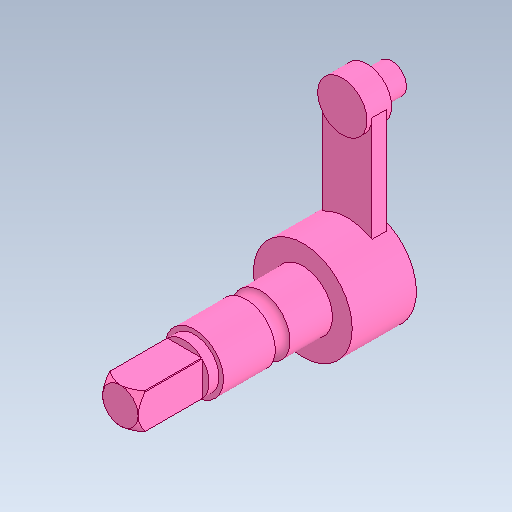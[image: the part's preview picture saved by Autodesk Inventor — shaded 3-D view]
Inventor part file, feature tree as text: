
AUTODESK INVENTOR PART (.ipt)
format: ipt  version: 2020.5 (Build 245400000, 400)  size: 203,264 bytes
history: native  units: mm
features: sketch x9, extrude x8, other x2, mirror x1, chamfer x1, revolve x1, projected_geometry x1
ambient origin geometry x8: Origin, YZ Plane, XZ Plane, XY Plane, X Axis, Y Axis, Z Axis, Center Point
bodies: Solid1 (feature_tree)
feature tree (23):
  extrude  "Extrusion1"  Depth=6.0mm
  extrude  "Extrusion2"  Depth=12.0mm
  mirror  "Mirror1"
  extrude  "Extrusion3"  Depth=5.0mm TaperAngle=0.0deg
  extrude  "Extrusion4"  Depth=3.0mm TaperAngle=0.0deg
  extrude  "Extrusion5"  Depth=35.0mm TaperAngle=0.0deg
  extrude  "Extrusion6"  Depth=5.0mm TaperAngle=0.0deg
  chamfer  "Chamfer1"  Distance=15.0mm
  extrude  "Extrusion7"  Depth=13.0mm TaperAngle=0.0deg
  other  "Work Point1"
  sketch  "Sketch8"  dims[d18=10.0mm d19=15.0mm d20=0.0mm]
  revolve  "Revolution1"  [1 undecoded]
  extrude  "Extrusion8"  TaperAngle=90.0deg  [1 undecoded]
  sketch  "Sketch1"  dims[d0=30.0mm d1=6.0mm]
  sketch  "Sketch2"  dims[d2=10.0mm d3=12.0mm]
  sketch  "Sketch3"  dims[d4=20.0mm d6=5.0mm d7=0.0mm]
  sketch  "Sketch4"  dims[d8=1.0mm d9=0.0mm d10=3.0mm d11=0.0mm]
  sketch  "Sketch5"  dims[d12=0.1mm d13=35.0mm d14=0.0mm]
  sketch  "Sketch6"  dims[d15=6.0mm d16=5.0mm d17=0.0mm]
  other  "Work Axis1"
  sketch  "Sketch9"  dims[d21=1.4mm d22=2.0mm d23=45.0deg d24=13.0mm d25=0.0mm]
  sketch  "Sketch10"  dims[d26=3.0mm d27=12.0mm d28=90.0deg d29=5.0mm d30=0.0mm]
  projected_geometry  "Projected Loop1"
note: 2 required parameter values undecoded (feature->parameter linkage not recoverable at this tier; creation-order binding heuristic only, values carry confidence <= 0.55)